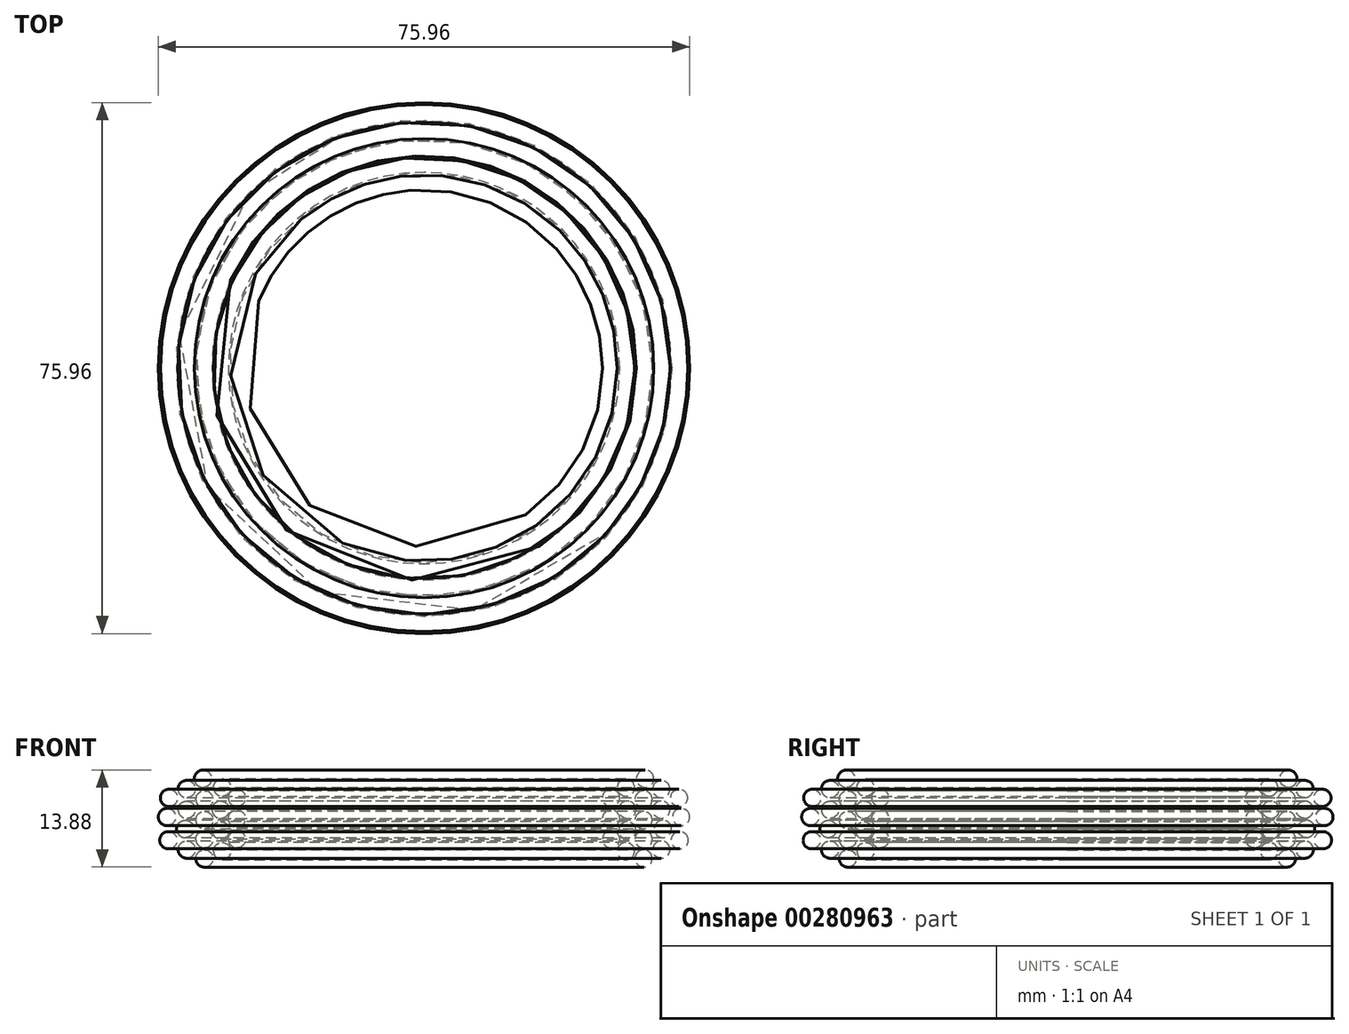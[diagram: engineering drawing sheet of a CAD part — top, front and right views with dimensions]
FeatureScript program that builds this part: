
annotation { "Feature Type Name" : "Feature", "Feature Type Description" : "" }
export const myFeature = defineFeature(function(context is Context, id is Id, definition is map)
    precondition{}
    {
        {
            var Q0;
            Q0=qCreatedBy(makeId("Front.planeOp"),FACE);
            var sketch = newSketch(context, id + "F0", { "sketchPlane" : qUnion([Q0])});
            skCircle(sketch, "E0", {"center": v(-31.4, 39.63) * mm, "radius": 1.23 * mm});
            skCircle(sketch, "E1", {"center": v(-31.4, 34.14) * mm, "radius": 1.23 * mm});
            skCircle(sketch, "E2", {"center": v(-36.75, 40.08) * mm, "radius": 1.23 * mm});
            skCircle(sketch, "E3", {"center": v(-36.46, 42.8) * mm, "radius": 1.23 * mm});
            skCircle(sketch, "E4", {"center": v(-33.93, 44.07) * mm, "radius": 1.23 * mm});
            skCircle(sketch, "E5", {"center": v(-33.93, 35.4) * mm, "radius": 1.23 * mm});
            skCircle(sketch, "E6", {"center": v(-26.74, 42.8) * mm, "radius": 1.23 * mm});
            skCircle(sketch, "E7", {"center": v(-36.54, 36.75) * mm, "radius": 1.23 * mm});
            skCircle(sketch, "E8", {"center": v(-31.6, 45.55) * mm, "radius": 1.23 * mm});
            skCircle(sketch, "E9", {"center": v(-28.85, 35.2) * mm, "radius": 1.23 * mm});
            skCircle(sketch, "E10", {"center": v(-29.07, 38.15) * mm, "radius": 1.23 * mm});
            skCircle(sketch, "E11", {"center": v(-26.74, 36.89) * mm, "radius": 1.23 * mm});
            skCircle(sketch, "E12", {"center": v(-33.93, 41.11) * mm, "radius": 1.23 * mm});
            skCircle(sketch, "E13", {"center": v(-29.07, 41.11) * mm, "radius": 1.23 * mm});
            skCircle(sketch, "E14", {"center": v(-28.85, 44.28) * mm, "radius": 1.23 * mm});
            skCircle(sketch, "E15", {"center": v(-26.74, 39.85) * mm, "radius": 1.23 * mm});
            skCircle(sketch, "E16", {"center": v(-34.14, 38.37) * mm, "radius": 1.23 * mm});
            skCircle(sketch, "E17", {"center": v(-31.4, 42.6) * mm, "radius": 1.23 * mm});
            skCircle(sketch, "E18", {"center": v(-31.4, 36.89) * mm, "radius": 1.23 * mm});
            skLineSegment(sketch, "E19", {"start": v(0, 50.69) * mm, "end": v(0, 23.43) * mm, "construction": true});
            skSolve(sketch);
        }
        {
            var Q0;
            Q0=makeQuery(id+"F0.imprint","IMPRINT",FACE,{"disambiguationData":[TD([[makeQuery(id+"F0.imprint","IMPRINT",EDGE,{"derivedFrom":sQuery(id+"F0.wireOp",EDGE,"E18")}),1.0]])]});
            var Q1;
            Q1=makeQuery(id+"F0.imprint","IMPRINT",FACE,{"disambiguationData":[TD([[makeQuery(id+"F0.imprint","IMPRINT",EDGE,{"derivedFrom":sQuery(id+"F0.wireOp",EDGE,"E9")}),1.0]])]});
            var Q2;
            Q2=makeQuery(id+"F0.imprint","IMPRINT",FACE,{"disambiguationData":[TD([[makeQuery(id+"F0.imprint","IMPRINT",EDGE,{"derivedFrom":sQuery(id+"F0.wireOp",EDGE,"E15")}),1.0]])]});
            var Q3;
            Q3=makeQuery(id+"F0.imprint","IMPRINT",FACE,{"disambiguationData":[TD([[makeQuery(id+"F0.imprint","IMPRINT",EDGE,{"derivedFrom":sQuery(id+"F0.wireOp",EDGE,"E17")}),1.0]])]});
            var Q4;
            Q4=makeQuery(id+"F0.imprint","IMPRINT",FACE,{"disambiguationData":[TD([[makeQuery(id+"F0.imprint","IMPRINT",EDGE,{"derivedFrom":sQuery(id+"F0.wireOp",EDGE,"E11")}),1.0]])]});
            var Q5;
            Q5=makeQuery(id+"F0.imprint","IMPRINT",FACE,{"disambiguationData":[TD([[makeQuery(id+"F0.imprint","IMPRINT",EDGE,{"derivedFrom":sQuery(id+"F0.wireOp",EDGE,"E12")}),1.0]])]});
            var Q6;
            Q6=makeQuery(id+"F0.imprint","IMPRINT",FACE,{"disambiguationData":[TD([[makeQuery(id+"F0.imprint","IMPRINT",EDGE,{"derivedFrom":sQuery(id+"F0.wireOp",EDGE,"E10")}),1.0]])]});
            var Q7;
            Q7=makeQuery(id+"F0.imprint","IMPRINT",FACE,{"disambiguationData":[TD([[makeQuery(id+"F0.imprint","IMPRINT",EDGE,{"derivedFrom":sQuery(id+"F0.wireOp",EDGE,"E7")}),1.0]])]});
            var Q8;
            Q8=makeQuery(id+"F0.imprint","IMPRINT",FACE,{"disambiguationData":[TD([[makeQuery(id+"F0.imprint","IMPRINT",EDGE,{"derivedFrom":sQuery(id+"F0.wireOp",EDGE,"E8")}),1.0]])]});
            var Q9;
            Q9=makeQuery(id+"F0.imprint","IMPRINT",FACE,{"disambiguationData":[TD([[makeQuery(id+"F0.imprint","IMPRINT",EDGE,{"derivedFrom":sQuery(id+"F0.wireOp",EDGE,"E6")}),1.0]])]});
            var Q10;
            Q10=makeQuery(id+"F0.imprint","IMPRINT",FACE,{"disambiguationData":[TD([[makeQuery(id+"F0.imprint","IMPRINT",EDGE,{"derivedFrom":sQuery(id+"F0.wireOp",EDGE,"E5")}),1.0]])]});
            var Q11;
            Q11=makeQuery(id+"F0.imprint","IMPRINT",FACE,{"disambiguationData":[TD([[makeQuery(id+"F0.imprint","IMPRINT",EDGE,{"derivedFrom":sQuery(id+"F0.wireOp",EDGE,"E4")}),1.0]])]});
            var Q12;
            Q12=makeQuery(id+"F0.imprint","IMPRINT",FACE,{"disambiguationData":[TD([[makeQuery(id+"F0.imprint","IMPRINT",EDGE,{"derivedFrom":sQuery(id+"F0.wireOp",EDGE,"E3")}),1.0]])]});
            var Q13;
            Q13=makeQuery(id+"F0.imprint","IMPRINT",FACE,{"disambiguationData":[TD([[makeQuery(id+"F0.imprint","IMPRINT",EDGE,{"derivedFrom":sQuery(id+"F0.wireOp",EDGE,"E2")}),1.0]])]});
            var Q14;
            Q14=makeQuery(id+"F0.imprint","IMPRINT",FACE,{"disambiguationData":[TD([[makeQuery(id+"F0.imprint","IMPRINT",EDGE,{"derivedFrom":sQuery(id+"F0.wireOp",EDGE,"E1")}),1.0]])]});
            var Q15;
            Q15=makeQuery(id+"F0.imprint","IMPRINT",FACE,{"disambiguationData":[TD([[makeQuery(id+"F0.imprint","IMPRINT",EDGE,{"derivedFrom":sQuery(id+"F0.wireOp",EDGE,"E0")}),1.0]])]});
            var Q16;
            Q16=makeQuery(id+"F0.imprint","IMPRINT",FACE,{"disambiguationData":[TD([[makeQuery(id+"F0.imprint","IMPRINT",EDGE,{"derivedFrom":sQuery(id+"F0.wireOp",EDGE,"E14")}),1.0]])]});
            var Q17;
            Q17=makeQuery(id+"F0.imprint","IMPRINT",FACE,{"disambiguationData":[TD([[makeQuery(id+"F0.imprint","IMPRINT",EDGE,{"derivedFrom":sQuery(id+"F0.wireOp",EDGE,"E16")}),1.0]])]});
            var Q18;
            Q18=makeQuery(id+"F0.imprint","IMPRINT",FACE,{"disambiguationData":[TD([[makeQuery(id+"F0.imprint","IMPRINT",EDGE,{"derivedFrom":sQuery(id+"F0.wireOp",EDGE,"E13")}),1.0]])]});
            var Q19;
            Q19=sQuery(id+"F0.wireOp",EDGE,"E19");
            revolve(context, id + "F1", {"entities" : qUnion([Q0, Q1, Q2, Q3, Q4, Q5, Q6, Q7, Q8, Q9, Q10, Q11, Q12, Q13, Q14, Q15, Q16, Q17, Q18]), "axis" : qUnion([Q19]), "revolveType" : RevolveType.FULL});
        }
    });
